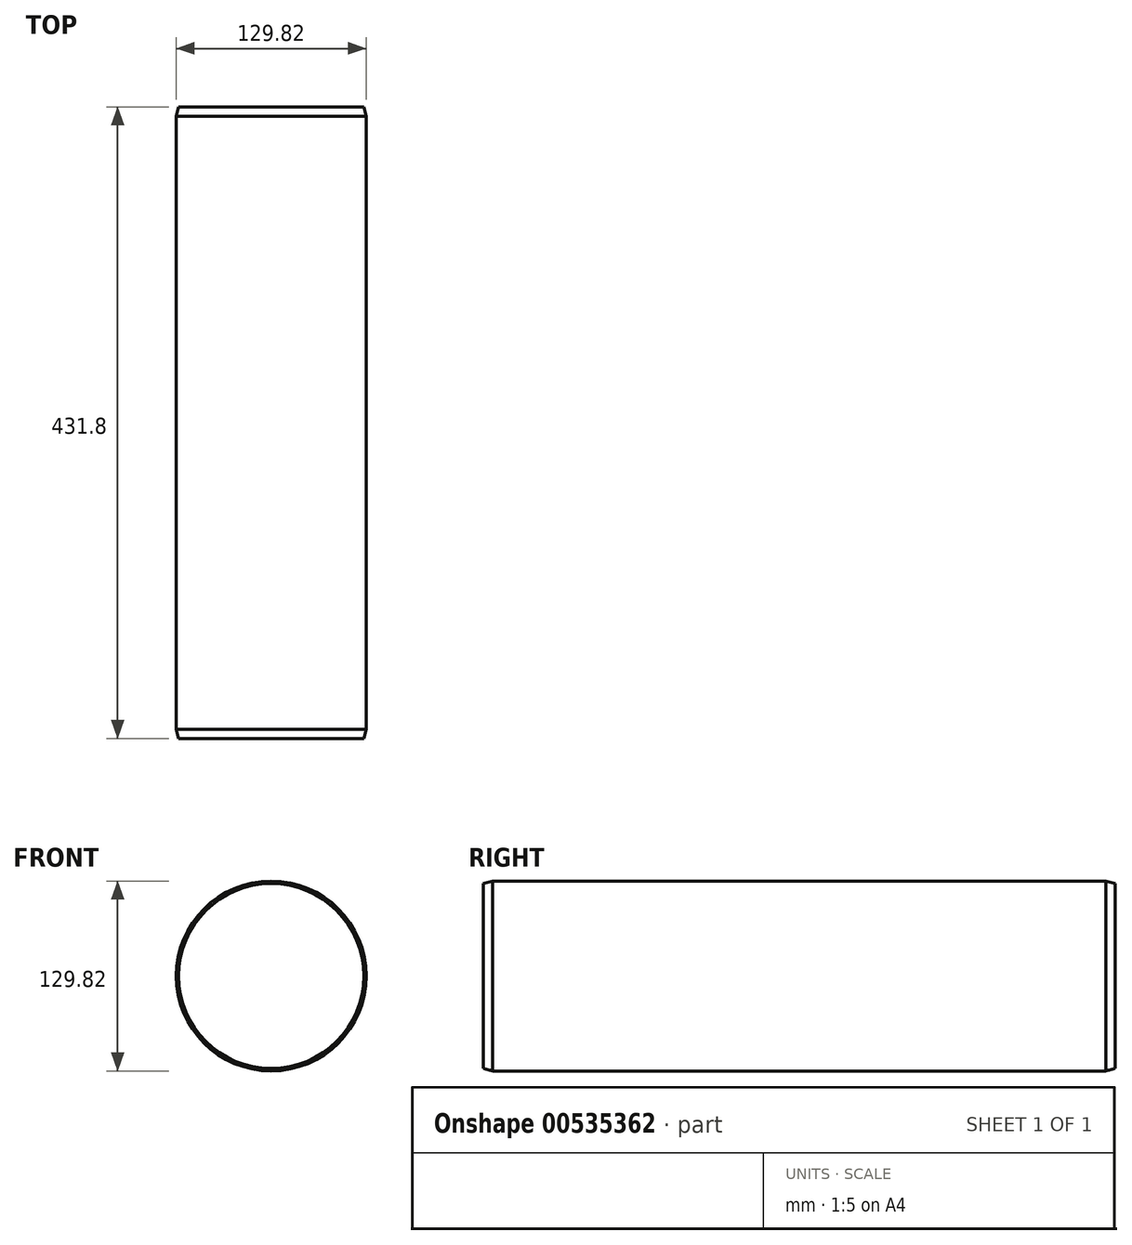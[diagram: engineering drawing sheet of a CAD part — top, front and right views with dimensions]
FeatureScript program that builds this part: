
annotation { "Feature Type Name" : "Feature", "Feature Type Description" : "" }
export const myFeature = defineFeature(function(context is Context, id is Id, definition is map)
    precondition{}
    {
        {
            var Q0;
            Q0=qCreatedBy(makeId("Front.planeOp"),FACE);
            var sketch = newSketch(context, id + "F0", { "sketchPlane" : qUnion([Q0])});
            skCircle(sketch, "E0", {"center": v(0, 0) * mm, "radius": 64.9 * mm});
            skSolve(sketch);
        }
        {
            var Q0;
            Q0=qSketchRegion(id+"F0",true);
            extrude(context, id + "F1", {"entities" : qUnion([Q0]), "depth" : 431.8 * mm, "offsetDistance" : 25.4 * mm});
        }
        {
            var Q0;
            Q0=makeQuery(id+"F1.opExtrude","CAP_EDGE",EDGE,{"disambiguationData":[OSD([sQuery(id+"F0.wireOp",EDGE,"E0")])],"isStart":false});
            var Q1;
            Q1=makeQuery(id+"F1.opExtrude","CAP_EDGE",EDGE,{"disambiguationData":[OSD([sQuery(id+"F0.wireOp",EDGE,"E0")])],"isStart":true});
            chamfer(context, id + "F2", {"entities" : qUnion([Q0, Q1]), "chamferType" : ChamferType.OFFSET_ANGLE, "width" : 6.35 * mm, "oppositeDirection" : true, "angle" : 15 * degree, "tangentPropagation" : true});
        }
    });
